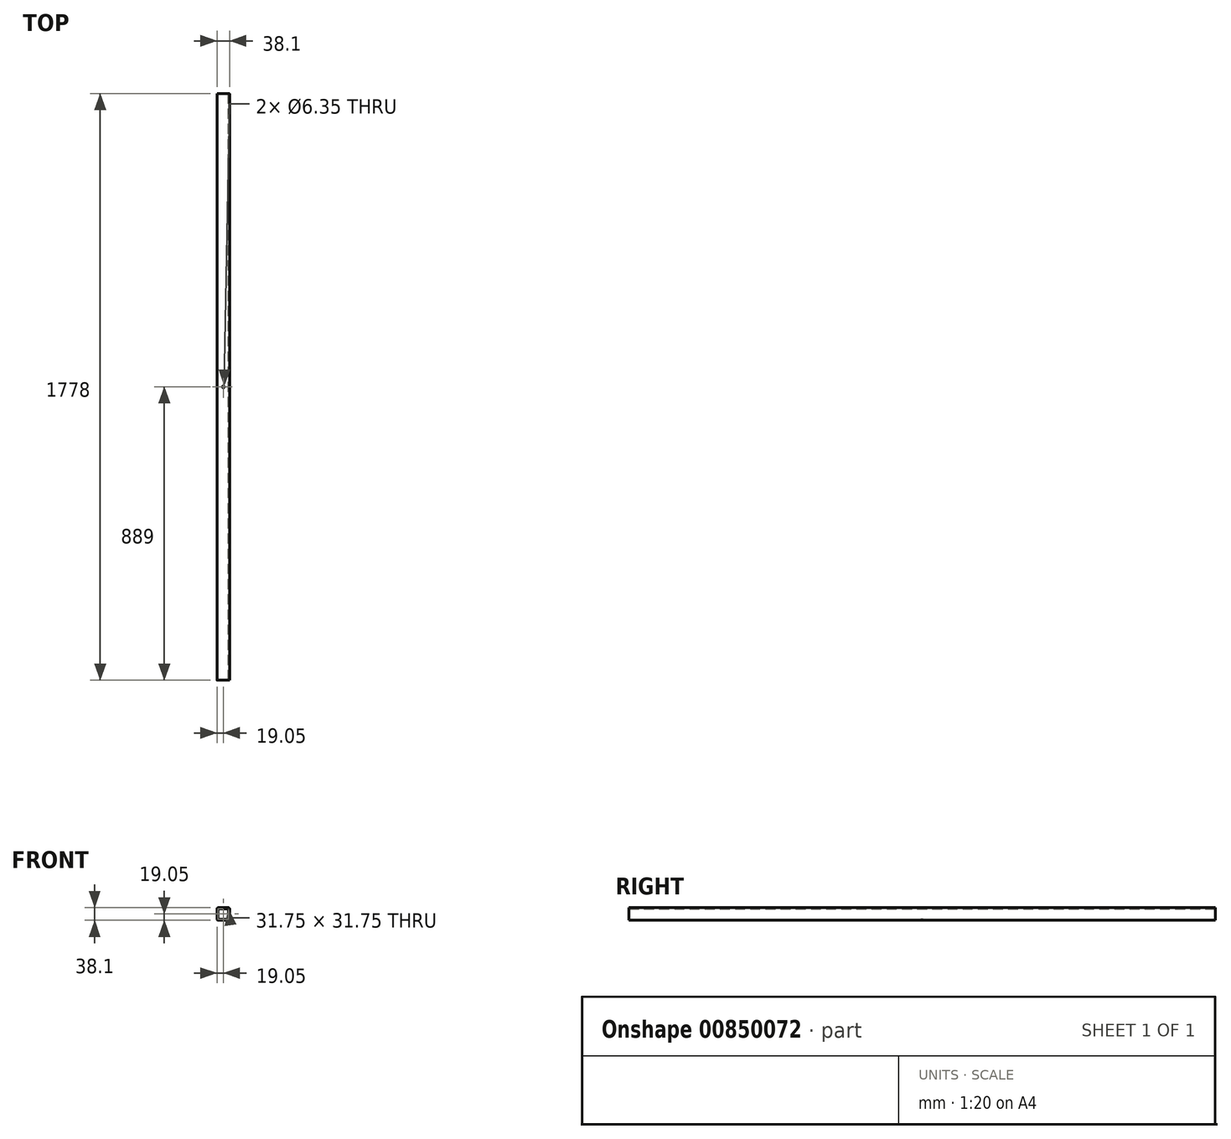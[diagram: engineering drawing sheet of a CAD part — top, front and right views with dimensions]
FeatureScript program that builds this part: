
annotation { "Feature Type Name" : "Feature", "Feature Type Description" : "" }
export const myFeature = defineFeature(function(context is Context, id is Id, definition is map)
    precondition{}
    {
        {
            var Q0;
            Q0=qCreatedBy(makeId("Front.planeOp"),FACE);
            var sketch = newSketch(context, id + "F0", { "sketchPlane" : qUnion([Q0])});
            skLineSegment(sketch, "E0.bottom", {"start": v(-15.88, -15.88) * mm, "end": v(15.88, -15.88) * mm});
            skLineSegment(sketch, "E0.top", {"start": v(-15.88, 15.88) * mm, "end": v(15.87, 15.88) * mm});
            skLineSegment(sketch, "E0.left", {"start": v(-15.87, -15.88) * mm, "end": v(-15.88, 15.88) * mm});
            skLineSegment(sketch, "E0.right", {"start": v(15.88, -15.88) * mm, "end": v(15.87, 15.88) * mm});
            skPoint(sketch, "E0.middle", {"position": v(0, 0) * mm});
            skLineSegment(sketch, "E1.bottom", {"start": v(-19.05, -19.05) * mm, "end": v(19.05, -19.05) * mm});
            skLineSegment(sketch, "E1.top", {"start": v(-19.05, 19.05) * mm, "end": v(19.05, 19.05) * mm});
            skLineSegment(sketch, "E1.left", {"start": v(-19.05, -19.05) * mm, "end": v(-19.05, 19.05) * mm});
            skLineSegment(sketch, "E1.right", {"start": v(19.05, -19.05) * mm, "end": v(19.05, 19.05) * mm});
            skSolve(sketch);
        }
        {
            var Q0;
            Q0 = qSketchRegion(id + "F0", true);
            extrude(context, id + "F1", {"entities" : qUnion([Q0]), "depth" : 1778 * mm, "offsetDistance" : 25.4 * mm});
        }
        {
            var Q0;
            Q0=makeQuery(id+"F1.opExtrude","SWEPT_EDGE",EDGE,{"disambiguationData":[OSD([sQuery(id+"F0.wireOp",EDGE,"E1.top"),sQuery(id+"F0.wireOp",EDGE,"E1.right")])]});
            var Q1;
            Q1=makeQuery(id+"F1.opExtrude","SWEPT_EDGE",EDGE,{"disambiguationData":[OSD([sQuery(id+"F0.wireOp",EDGE,"E1.bottom"),sQuery(id+"F0.wireOp",EDGE,"E1.right")])]});
            var Q2;
            Q2=makeQuery(id+"F1.opExtrude","SWEPT_EDGE",EDGE,{"disambiguationData":[OSD([sQuery(id+"F0.wireOp",EDGE,"E1.bottom"),sQuery(id+"F0.wireOp",EDGE,"E1.left")])]});
            var Q3;
            Q3=makeQuery(id+"F1.opExtrude","SWEPT_EDGE",EDGE,{"disambiguationData":[OSD([sQuery(id+"F0.wireOp",EDGE,"E1.top"),sQuery(id+"F0.wireOp",EDGE,"E1.left")])]});
            fillet(context, id + "F2", {"entities" : qUnion([Q0, Q1, Q2, Q3]), "radius" : 3.17 * mm, "tangentPropagation" : true, "allowEdgeOverflow" : false});
        }
        {
            var Q0;
            Q0=makeQuery(id+"F1.opExtrude","SWEPT_FACE",FACE,{"disambiguationData":[OSD([sQuery(id+"F0.wireOp",EDGE,"E1.top")])]});
            var sketch = newSketch(context, id + "F3", { "sketchPlane" : qUnion([Q0])});
            skLineSegment(sketch, "E2", {"start": v(0, 0) * mm, "end": v(0, -889) * mm});
            skCircle(sketch, "E3", {"center": v(0, -889) * mm, "radius": 3.18 * mm});
            skSolve(sketch);
        }
        {
            var Q0;
            Q0 = qSketchRegion(id + "F3", true);
            extrude(context, id + "F4", {"entities" : qUnion([Q0]), "operationType" : NewBodyOperationType.REMOVE, "endBound" : BoundingType.THROUGH_ALL, "oppositeDirection" : true, "depth" : 25.4 * mm, "offsetDistance" : 25.4 * mm});
        }
    });
